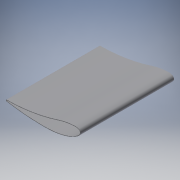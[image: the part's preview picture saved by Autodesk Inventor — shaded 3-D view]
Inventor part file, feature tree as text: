
AUTODESK INVENTOR PART (.ipt)
format: ipt  version: 2018.2 (Build 222227000, 227)  size: 130,560 bytes
history: native  units: mm
features: extrude x1, shell x1, sketch x1, projected_geometry x1
ambient origin geometry x8: Origin, YZ Plane, XZ Plane, XY Plane, X Axis, Y Axis, Z Axis, Center Point
bodies: Body1 (feature_tree)
feature tree (4):
  extrude  "押し出し1"  Depth=186.0mm TaperAngle=0.0deg
  shell  "シェル1"  Thickness=1.0mm
  sketch  "スケッチ1"
  projected_geometry  "投影ループ1"
